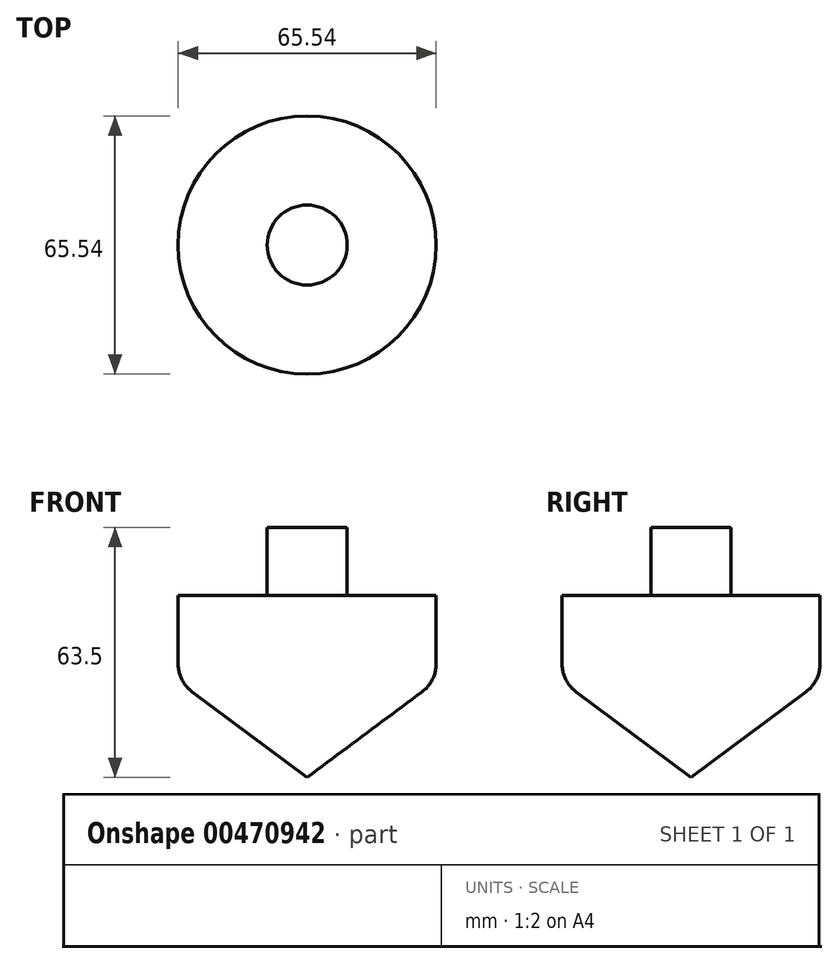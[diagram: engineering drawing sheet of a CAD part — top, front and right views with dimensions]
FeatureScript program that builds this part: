
annotation { "Feature Type Name" : "Feature", "Feature Type Description" : "" }
export const myFeature = defineFeature(function(context is Context, id is Id, definition is map)
    precondition{}
    {
        {
            var Q0;
            Q0=qCreatedBy(makeId("Front.planeOp"),FACE);
            var sketch = newSketch(context, id + "F0", { "sketchPlane" : qUnion([Q0])});
            skLineSegment(sketch, "E0", {"start": v(10.16, 46.2) * mm, "end": v(10.16, 63.5) * mm});
            skLineSegment(sketch, "E1", {"start": v(10.16, 63.5) * mm, "end": v(0, 63.5) * mm});
            skLineSegment(sketch, "E2", {"start": v(0, 63.5) * mm, "end": v(0, 0) * mm});
            skLineSegment(sketch, "E3", {"start": v(32.77, 28.87) * mm, "end": v(32.77, 46.2) * mm});
            skLineSegment(sketch, "E4", {"start": v(0, 0) * mm, "end": v(29.2, 21.73) * mm});
            skLineSegment(sketch, "E5", {"start": v(10.16, 46.2) * mm, "end": v(32.77, 46.2) * mm});
            skLineSegment(sketch, "E6", {"start": v(32.77, 46.2) * mm, "end": v(32.77, 28.87) * mm});
            skArc(sketch, "E7.filletArc", {"start": v(29.2, 21.73) * mm, "mid": v(31.83, 24.88) * mm, "end": v(32.77, 28.87) * mm});
            skSolve(sketch);
        }
        {
            var Q0;
            Q0 = qSketchRegion(id + "F0", true);
            var Q1;
            Q1=sQuery(id+"F0.wireOp",EDGE,"E2");
            revolve(context, id + "F1", {"entities" : qUnion([Q0]), "axis" : qUnion([Q1]), "revolveType" : RevolveType.FULL});
        }
    });
